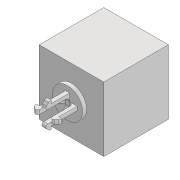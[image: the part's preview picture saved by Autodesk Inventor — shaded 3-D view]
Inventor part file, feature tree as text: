
AUTODESK INVENTOR PART (.ipt)
format: ipt  version: 2020.2 (Build 242310000, 310)  size: 542,720 bytes
history: native  units: in
note: dims shown in document units (in); Inventor stores cm internally (conversion verified against a paired STEP export)
features: sketch x9, extrude x9, fillet x7, projected_geometry x3, other x3, plane x2, reference x2, chamfer x1
ambient origin geometry x8: Origin, YZ Plane, XZ Plane, XY Plane, X Axis, Y Axis, Z Axis, Center Point
bodies: Solid1 (feature_tree)
feature tree (36):
  sketch  "Sketch1"  dims[d1=0.005in d2=1.0in d3=0.0in]
  plane  "Work Plane1"
  extrude  "Extrusion1"  Depth=1.0in TaperAngle=0.0deg
  extrude  "Extrusion2"  Depth=1.0in
  extrude  "Extrusion3"  TaperAngle=0.0deg  [1 undecoded]
  extrude  "Extrusion4"  Depth=0.01in TaperAngle=0.0deg
  extrude  "Extrusion5"  Depth=0.1in TaperAngle=45.0deg
  chamfer  "Chamfer1"  Distance=0.0625in
  extrude  "Extrusion6"  Depth=1.0in
  sketch  "Sketch7"  dims[d19=0.0in]
  plane  "Work Plane2"
  extrude  "Extrusion7"  TaperAngle=0.0deg  [1 undecoded]
  fillet  "Fillet1"  [1 undecoded]
  fillet  "Fillet2"  Radius=1.0in
  fillet  "Fillet3"  Radius=1.0in
  extrude  "Extrusion8"  Depth=0.032in
  fillet  "Fillet4"  Radius=0.06in
  fillet  "Fillet5"  Radius=0.0625in
  extrude  "Extrusion9"  Depth=1.0in
  fillet  "Fillet6"  Radius=0.3937in
  fillet  "Fillet7"  Radius=0.01in
  reference  "Reference1"
  sketch  "Sketch2"  dims[d4=0.0625in d5=0.0in d6=1.0in]
  reference  "Reference2"
  sketch  "Sketch3"  dims[d7=0.0in d8=0.0in]
  projected_geometry  "Projected Loop1"
  sketch  "Sketch4"  dims[d9=1.0in d10=0.0in d11=0.01in d12=0.0in]
  sketch  "Sketch5"  dims[d13=0.125in d14=0.0in d15=0.1in d16=0.125in d17=45.0deg]
  sketch  "Sketch6"  dims[d18=0.0625in]
  projected_geometry  "Projected Loop2"
  sketch  "Sketch8"  dims[d20=0.0in]
  projected_geometry  "Projected Loop3"
  sketch  "Sketch9"  dims[d21=1.0in d22=0.0625in d23=1.0in d24=0.0in d25=0.0in d26=1.0in d27=0.0in d28=1.0in d29=0.0in d30=0.032in d31=0.06in d32=0.0625in d33=1.0in d34=0.3937in d35=0.01in d36=0.0in d37=0.0in d38=0.5in d39=0.5in d40=0.2in d41=0.0in d42=0.0in d43=0.0625in d44=0.1in]
  parser-record x1  (decoder bookkeeping rows leaked as tree rows — omitted from the tree; the rows remain in map.json)
  other  "Assembly1.iam"
  other  "bearing_1:1"
note: 3 required parameter values undecoded (feature->parameter linkage not recoverable at this tier; creation-order binding heuristic only, values carry confidence <= 0.55)
note: 1 file-system path scrubbed to <path> (originals preserved in map.json)
